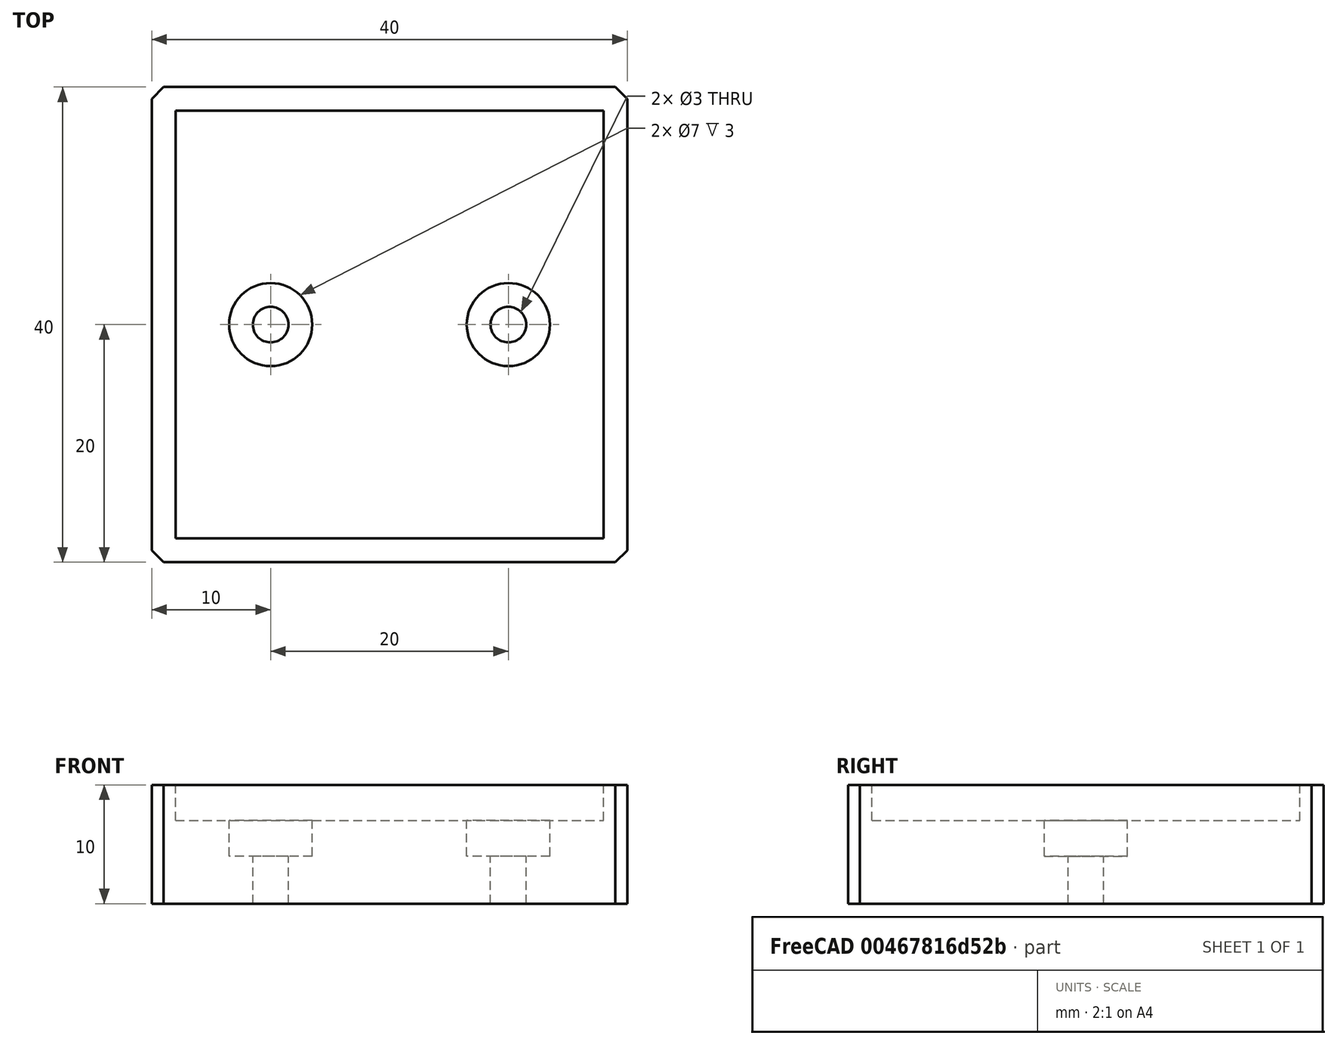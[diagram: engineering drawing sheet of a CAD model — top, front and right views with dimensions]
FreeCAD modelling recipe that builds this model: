
FCSTD DOCUMENT  (FreeCAD 0.18R14555 (Git shallow))
Label: damper-feet-2
License: All rights reserved
LicenseURL: http://en.wikipedia.org/wiki/All_rights_reserved
objects: Part::Cylinder×4, Part::Box×2, Part::Cut×2, Part::MultiFuse×1, Part::Chamfer×1, Part::Feature×1
note: 11 computed .brp shape members not serialized (recipe doc carries the construction recipe); baked Part::Feature solids carry a one-line shape summary decoded from their .brp

FEATURE [Part::Box] Box  label="Cube"
  AttacherType = Attacher::AttachEngine3D
  Height = 10
  Length = 40
  Width = 40
FEATURE [Part::Box] Box001  label="Cube001"
  AttacherType = Attacher::AttachEngine3D
  Height = 3
  Length = 36
  Placement = pos=(2,2,7) rot=(0,0,1;0rad)
  Width = 36
FEATURE [Part::Cut] Cut
  Base = -> Box
  Tool = -> Box001
FEATURE [Part::Cylinder] Cylinder
  Angle = 360
  AttacherType = Attacher::AttachEngine3D
  Height = 7
  Placement = pos=(30,20,0) rot=(0,0,1;0rad)
  Radius = 1.5
FEATURE [Part::Cylinder] Cylinder001
  Angle = 360
  AttacherType = Attacher::AttachEngine3D
  Height = 7
  Placement = pos=(10,20,0) rot=(0,0,1;0rad)
  Radius = 1.5
FEATURE [Part::Cylinder] Cylinder002
  Angle = 360
  AttacherType = Attacher::AttachEngine3D
  Height = 3
  Placement = pos=(10,20,4) rot=(0,0,1;0rad)
  Radius = 3.5
FEATURE [Part::Cylinder] Cylinder003
  Angle = 360
  AttacherType = Attacher::AttachEngine3D
  Height = 3
  Placement = pos=(30,20,4) rot=(0,0,1;0rad)
  Radius = 3.5
FEATURE [Part::MultiFuse] Fusion
  Shapes = -> [Cylinder001,Cylinder002,Cylinder003,Cylinder]
FEATURE [Part::Cut] Cut001
  Base = -> Cut
  Tool = -> Fusion
FEATURE [Part::Chamfer] Chamfer
  Base = -> Cut001
  Edges = 4 edges r=1: [Edge1,Edge3,Edge6,Edge15]
FEATURE [Part::Feature] Chamfer_solid  label="Chamfer (Solid)"
  shape: bbox 40 x 40 x 10 mm, 21 faces (baked)
